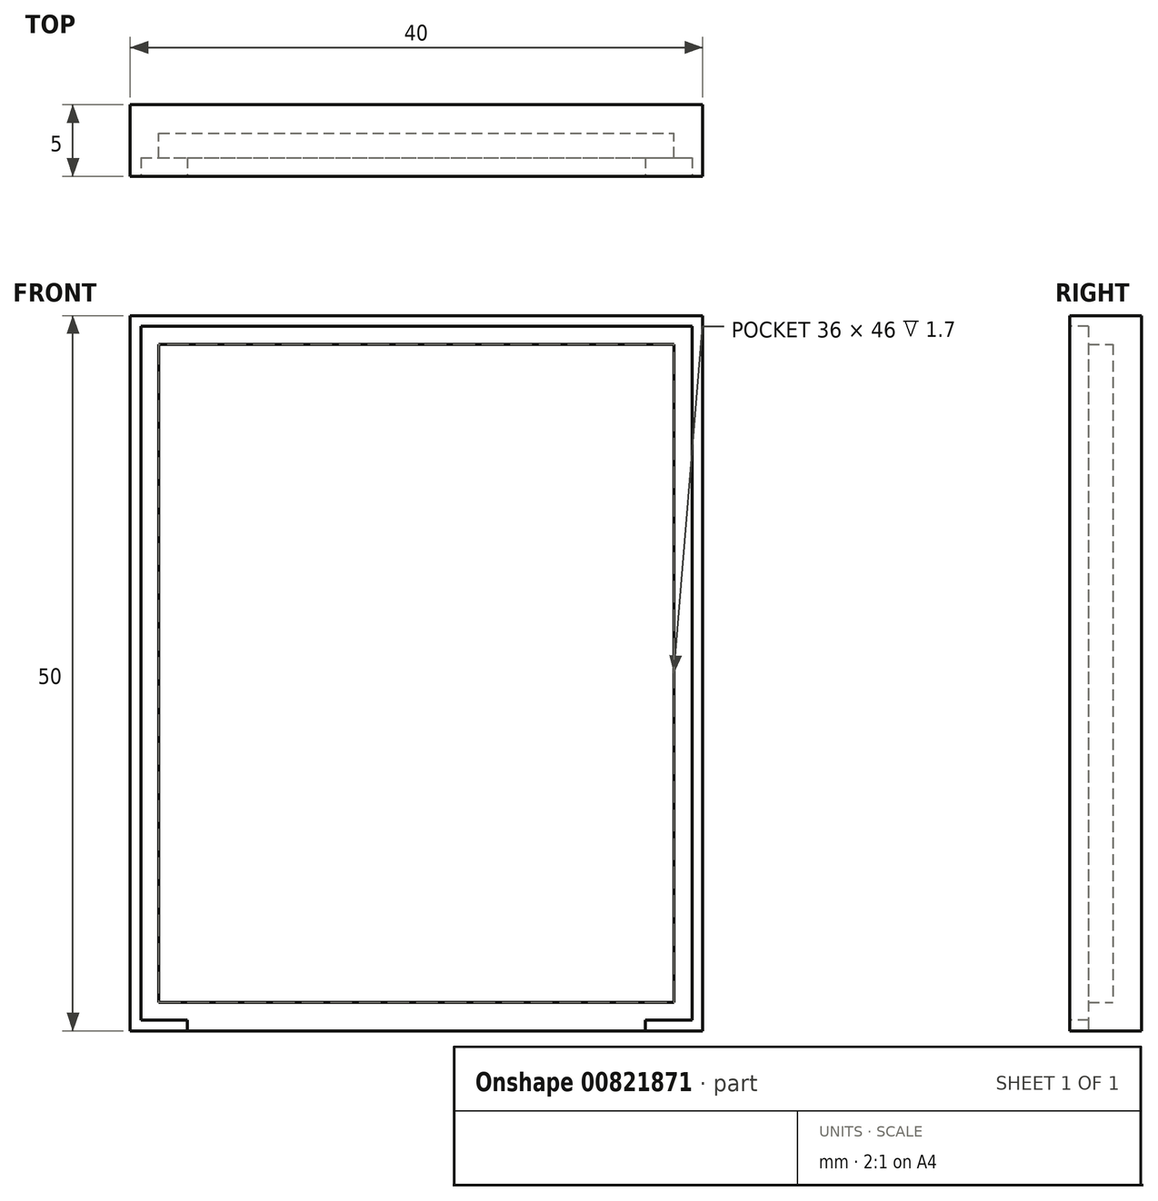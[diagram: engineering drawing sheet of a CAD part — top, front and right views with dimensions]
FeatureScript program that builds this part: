
annotation { "Feature Type Name" : "Feature", "Feature Type Description" : "" }
export const myFeature = defineFeature(function(context is Context, id is Id, definition is map)
    precondition{}
    {
        {
            var Q0;
            Q0=qCreatedBy(makeId("Front.planeOp"),FACE);
            var sketch = newSketch(context, id + "F0", { "sketchPlane" : qUnion([Q0])});
            skLineSegment(sketch, "E0.bottom", {"start": v(-20, 25) * mm, "end": v(20, 25) * mm});
            skLineSegment(sketch, "E0.top", {"start": v(-20, -25) * mm, "end": v(20, -25) * mm});
            skLineSegment(sketch, "E0.left", {"start": v(-20, 25) * mm, "end": v(-20, -25) * mm});
            skLineSegment(sketch, "E0.right", {"start": v(20, 25) * mm, "end": v(20, -25) * mm});
            skPoint(sketch, "E0.middle", {"position": v(0, 0) * mm});
            skSolve(sketch);
        }
        {
            var Q0;
            Q0=makeQuery(id+"F0.imprint","IMPRINT",FACE,{"disambiguationData":[TD([[makeQuery(id+"F0.imprint","IMPRINT",EDGE,{"derivedFrom":sQuery(id+"F0.wireOp",EDGE,"E0.bottom")}),-1.0]])]});
            extrude(context, id + "F1", {"entities" : qUnion([Q0]), "depth" : 2 * mm, "offsetDistance" : 25 * mm});
        }
        {
            var Q0;
            Q0=makeQuery(id+"F1.opExtrude","CAP_FACE",FACE,{"disambiguationData":[OSD([sQuery(id+"F0.wireOp",EDGE,"E0.bottom"),sQuery(id+"F0.wireOp",EDGE,"E0.top"),sQuery(id+"F0.wireOp",EDGE,"E0.left"),sQuery(id+"F0.wireOp",EDGE,"E0.right")])],"isStart":false});
            var sketch = newSketch(context, id + "F2", { "sketchPlane" : qUnion([Q0])});
            skLineSegment(sketch, "E1.bottom", {"start": v(-18, 23) * mm, "end": v(18, 23) * mm});
            skLineSegment(sketch, "E1.top", {"start": v(-18, -23) * mm, "end": v(18, -23) * mm});
            skLineSegment(sketch, "E1.left", {"start": v(-18, 23) * mm, "end": v(-18, -23) * mm});
            skLineSegment(sketch, "E1.right", {"start": v(18, 23) * mm, "end": v(18, -23) * mm});
            skPoint(sketch, "E1.middle", {"position": v(0, 0) * mm});
            skSolve(sketch);
        }
        {
            var Q0;
            Q0=makeQuery(id+"F2.imprint","IMPRINT",FACE,{"disambiguationData":[TD([[makeQuery(id+"F2.imprint","IMPRINT",EDGE,{"derivedFrom":sQuery(id+"F2.wireOp",EDGE,"E1.bottom")}),1.0]])]});
            extrude(context, id + "F3", {"entities" : qUnion([Q0]), "operationType" : NewBodyOperationType.ADD, "depth" : 3 * mm, "offsetDistance" : 25 * mm});
        }
        {
            var Q0;
            Q0=makeQuery(id+"F3.opExtrude","CAP_FACE",FACE,{"disambiguationData":[OSD([sQuery(id+"F0.wireOp",EDGE,"E0.bottom"),sQuery(id+"F0.wireOp",EDGE,"E0.top"),sQuery(id+"F0.wireOp",EDGE,"E0.left"),sQuery(id+"F0.wireOp",EDGE,"E0.right"),sQuery(id+"F2.wireOp",EDGE,"E1.bottom"),sQuery(id+"F2.wireOp",EDGE,"E1.top"),sQuery(id+"F2.wireOp",EDGE,"E1.left"),sQuery(id+"F2.wireOp",EDGE,"E1.right")])],"isStart":false});
            var sketch = newSketch(context, id + "F4", { "sketchPlane" : qUnion([Q0])});
            skLineSegment(sketch, "E2.bottom", {"start": v(-19.25, 24.25) * mm, "end": v(19.25, 24.25) * mm});
            skLineSegment(sketch, "E2.top", {"start": v(-19.25, -24.25) * mm, "end": v(19.25, -24.25) * mm});
            skLineSegment(sketch, "E2.left", {"start": v(-19.25, 24.25) * mm, "end": v(-19.25, -24.25) * mm});
            skLineSegment(sketch, "E2.right", {"start": v(19.25, 24.25) * mm, "end": v(19.25, -24.25) * mm});
            skPoint(sketch, "E2.middle", {"position": v(0, 0) * mm});
            skLineSegment(sketch, "E3.0", {"start": v(-18, 23) * mm, "end": v(-18, -23) * mm});
            skLineSegment(sketch, "E3.1", {"start": v(-18, 23) * mm, "end": v(18, 23) * mm});
            skLineSegment(sketch, "E3.2", {"start": v(18, 23) * mm, "end": v(18, -23) * mm});
            skLineSegment(sketch, "E3.3", {"start": v(-18, -23) * mm, "end": v(18, -23) * mm});
            skSolve(sketch);
        }
        {
            var Q0;
            Q0=makeQuery(id+"F4.imprint","IMPRINT",FACE,{"disambiguationData":[TD([[makeQuery(id+"F4.imprint","IMPRINT",EDGE,{"derivedFrom":sQuery(id+"F4.wireOp",EDGE,"E2.bottom")}),-1.0]])]});
            extrude(context, id + "F5", {"entities" : qUnion([Q0]), "operationType" : NewBodyOperationType.REMOVE, "oppositeDirection" : true, "depth" : 1.3 * mm, "offsetDistance" : 25 * mm});
        }
        {
            var Q0;
            Q0=makeQuery(id+"F3.opExtrude","CAP_FACE",FACE,{"disambiguationData":[OSD([sQuery(id+"F0.wireOp",EDGE,"E0.bottom"),sQuery(id+"F0.wireOp",EDGE,"E0.top"),sQuery(id+"F0.wireOp",EDGE,"E0.left"),sQuery(id+"F0.wireOp",EDGE,"E0.right"),sQuery(id+"F2.wireOp",EDGE,"E1.bottom"),sQuery(id+"F2.wireOp",EDGE,"E1.top"),sQuery(id+"F2.wireOp",EDGE,"E1.left"),sQuery(id+"F2.wireOp",EDGE,"E1.right")])],"isStart":false});
            var sketch = newSketch(context, id + "F6", { "sketchPlane" : qUnion([Q0])});
            skLineSegment(sketch, "E4.0", {"start": v(-19.25, -24.25) * mm, "end": v(19.25, -24.25) * mm});
            skLineSegment(sketch, "E4.1", {"start": v(-20, -25) * mm, "end": v(20, -25) * mm});
            skLineSegment(sketch, "E5", {"start": v(-16, -24.25) * mm, "end": v(-16, -25) * mm});
            skLineSegment(sketch, "E6", {"start": v(16, -24.25) * mm, "end": v(16, -25) * mm});
            skSolve(sketch);
        }
        {
            var Q0;
            {var subQ0=sQuery(id+"F6.wireOp",EDGE,"E5");Q0=makeQuery(id+"F6.imprint","IMPRINT",FACE,{"disambiguationData":[TD([[makeQuery(id+"F6.imprint","IMPRINT",EDGE,{"derivedFrom":subQ0}),1.0]])]});}
            extrude(context, id + "F7", {"entities" : qUnion([Q0]), "operationType" : NewBodyOperationType.REMOVE, "oppositeDirection" : true, "depth" : 1.3 * mm, "offsetDistance" : 25 * mm});
        }
    });
